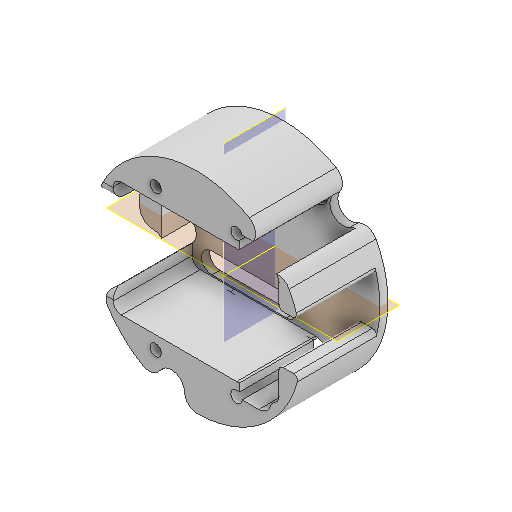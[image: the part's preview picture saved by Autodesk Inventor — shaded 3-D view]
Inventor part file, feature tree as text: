
AUTODESK INVENTOR PART (.ipt)
format: ipt  version: 2022 (Build 260153000, 153)  size: 337,408 bytes
history: native  units: in
note: dims shown in document units (in); Inventor stores cm internally (conversion verified against a paired STEP export)
features: other x8, sketch x8, extrude x7, fillet x5, reference x4, projected_geometry x3, plane x2, hole x1
ambient origin geometry x8: Origin, YZ Plane, XZ Plane, XY Plane, X Axis, Y Axis, Z Axis, Center Point
bodies: Body1 (feature_tree)
feature tree (38):
  extrude  "Extrusion5"  Depth=0.0787in TaperAngle=0.0deg
  extrude  "Extrusion6"  Depth=0.7677in
  fillet  "Fillet2"  Radius=0.7677in
  extrude  "Extrusion7"  Depth=0.4724in TaperAngle=0.0deg
  hole  "Hole2"  [1 undecoded]
  plane  "Work Plane4"
  plane  "Work Plane5"
  fillet  "Fillet4"  Radius=0.0394in
  other  "Work Axis1"
  extrude  "Extrusion8"  Depth=0.4724in
  fillet  "Fillet5"  Radius=0.4724in
  extrude  "Extrusion9"  Depth=1.0in TaperAngle=0.0deg
  extrude  "Extrusion10"  Depth=0.125in
  fillet  "Fillet6"  Radius=0.2559in
  extrude  "Extrusion11"  Depth=0.125in
  fillet  "Fillet7"  Radius=0.2559in
  sketch  "Sketch6"  dims[d33=2.0472in d34=0.0787in d35=0.0in]
  sketch  "Sketch7"  dims[d36=1.6142in d37=1.122in d38=0.7677in d39=0.0in]
  sketch  "Sketch8"  dims[d40=0.0787in d41=0.4724in d42=0.0in]
  projected_geometry  "Projected Loop5"
  sketch  "Sketch9"  dims[d44=0.7874in d45=1.378in]
  projected_geometry  "Projected Loop6"
  sketch  "Sketch11"  dims[d46=0.1102in d47=0.75in d48=0.2559in d49=0.1181in d50=0.5635in d51=1.0in d52=0.8108in d53=0.0394in]
  projected_geometry  "Projected Loop7"
  sketch  "Sketch12"  dims[d57=0.0in d58=0.0in d59=0.7087in d60=0.4724in]
  reference  "Reference5"
  reference  "Reference6"
  reference  "Reference7"
  reference  "Reference8"
  sketch  "Sketch13"  dims[d61=0.1181in d62=1.0in d63=0.0in]
  sketch  "Sketch14"  dims[d64=1.0in d65=0.0in d66=0.1181in d67=0.2559in d68=0.2559in d69=0.2559in d70=1.0in d71=0.0in d72=0.125in]
  other  "<userpath>\Documents\MANATEE\INVENTOR\MANATEE_V1.iam"
  other  "MANATEE_V1.iam"
  other  "00_ESP3-CAM:1"
  other  "Pin Header 4 x 1 TH 2.54mm Pitch v1:1"
  other  "Pin Header 4 x 1 TH 2.54mm Pitch v1:2"
  other  "Pin Header 4 x 1 TH 2.54mm Pitch v1:3"
  other  "Pin Header 4 x 1 TH 2.54mm Pitch v1:4"
note: 1 required parameter value undecoded (feature->parameter linkage not recoverable at this tier; creation-order binding heuristic only, values carry confidence <= 0.55)
